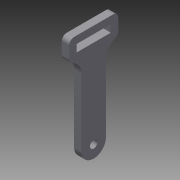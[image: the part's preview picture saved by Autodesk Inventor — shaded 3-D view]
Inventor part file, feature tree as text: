
AUTODESK INVENTOR PART (.ipt)
format: ipt  version: 2015 (Build 190159000, 159)  size: 115,712 bytes
history: native  units: mm
features: extrude x1, fillet x1, sketch x1
ambient origin geometry x8: Origin, YZ Plane, XZ Plane, XY Plane, X Axis, Y Axis, Z Axis, Center Point
bodies: Body1 (feature_tree)
feature tree (3):
  extrude  "Extrusion10"  Depth=10.0mm
  fillet  "Fillet1"  Radius=6.0mm
  sketch  "Sketch1"  dims[d8=22.5deg d16=3.0mm d25=10.0mm d32=6.0mm d33=6.0mm d70=38.0mm d74=22.5deg d81=90.0mm d82=46.0mm d90=2.0mm d93=1.0mm d95=22.5deg d109=3.0mm d112=36.0mm d113=5.0mm d115=20.0mm d118=6.0mm d120=6.0mm d122=3.0mm d123=0.0mm d124=2.0mm]
